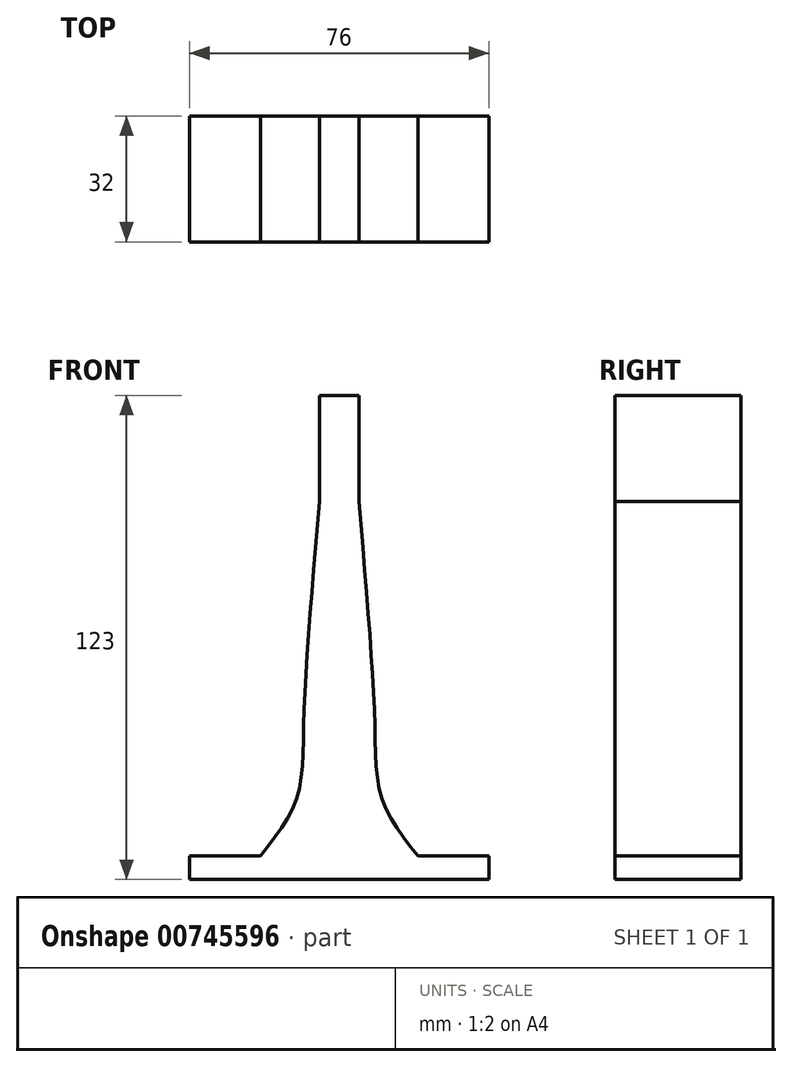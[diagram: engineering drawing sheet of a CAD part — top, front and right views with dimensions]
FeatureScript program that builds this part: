
annotation { "Feature Type Name" : "Feature", "Feature Type Description" : "" }
export const myFeature = defineFeature(function(context is Context, id is Id, definition is map)
    precondition{}
    {
        {
            var Q0;
            Q0=qCreatedBy(makeId("Front.planeOp"),FACE);
            var sketch = newSketch(context, id + "F0", { "sketchPlane" : qUnion([Q0])});
            skLineSegment(sketch, "E0", {"start": v(-38, -61.5) * mm, "end": v(38, -61.5) * mm});
            skLineSegment(sketch, "E1", {"start": v(38, -61.5) * mm, "end": v(38, -55.5) * mm});
            skLineSegment(sketch, "E2", {"start": v(38, -55.5) * mm, "end": v(-38, -55.5) * mm});
            skLineSegment(sketch, "E3", {"start": v(-38, -55.5) * mm, "end": v(-38, -61.5) * mm});
            skLineSegment(sketch, "E4", {"start": v(-5, 61.5) * mm, "end": v(5, 61.5) * mm});
            skFitSpline(sketch, "E5", {"points": [v(-5, 34.5) * mm, v(-9, -21.12) * mm, v(-11, -41.34) * mm, v(-20, -55.5) * mm]});
            skFitSpline(sketch, "E6", {"points": [v(5, 34.5) * mm, v(9, -21.12) * mm, v(11, -41.34) * mm, v(20, -55.5) * mm]});
            skLineSegment(sketch, "E7", {"start": v(5, 61.5) * mm, "end": v(5, -55.5) * mm});
            skLineSegment(sketch, "E8", {"start": v(-5, 61.5) * mm, "end": v(-5, -55.5) * mm});
            skSolve(sketch);
        }
        {
            var Q0;
            Q0=makeQuery(id+"F0.imprint","IMPRINT",FACE,{"disambiguationData":[TD([[makeQuery(id+"F0.imprint","IMPRINT",EDGE,{"derivedFrom":sQuery(id+"F0.wireOp",EDGE,"E0")}),1.0]])]});
            var Q1;
            {var subQ4=sQuery(id+"F0.wireOp",EDGE,"E4");Q1=makeQuery(id+"F0.imprint","IMPRINT",FACE,{"disambiguationData":[TD([[makeQuery(id+"F0.imprint","IMPRINT",EDGE,{"derivedFrom":subQ4}),-1.0]])]});}
            extrude(context, id + "F1", {"entities" : qUnion([Q0, Q1]), "depth" : 32 * mm, "offsetDistance" : 25 * mm});
        }
        {
            var Q0;
            Q0=qCreatedBy(makeId("Front.planeOp"),FACE);
            var sketch = newSketch(context, id + "F2", { "sketchPlane" : qUnion([Q0])});
            skLineSegment(sketch, "E9", {"start": v(-38, -61.5) * mm, "end": v(38, -61.5) * mm});
            skLineSegment(sketch, "E10", {"start": v(38, -61.5) * mm, "end": v(38, -55.5) * mm});
            skLineSegment(sketch, "E11", {"start": v(38, -55.5) * mm, "end": v(-38, -55.5) * mm});
            skLineSegment(sketch, "E12", {"start": v(-38, -55.5) * mm, "end": v(-38, -61.5) * mm});
            skLineSegment(sketch, "E13", {"start": v(-5, 61.5) * mm, "end": v(5, 61.5) * mm});
            skFitSpline(sketch, "E14", {"points": [v(-5, 34.5) * mm, v(-9, -21.12) * mm, v(-11, -41.34) * mm, v(-20, -55.5) * mm]});
            skFitSpline(sketch, "E15", {"points": [v(5, 34.5) * mm, v(9, -21.12) * mm, v(11, -41.34) * mm, v(20, -55.5) * mm]});
            skLineSegment(sketch, "E16", {"start": v(5, 61.5) * mm, "end": v(5, -55.5) * mm});
            skLineSegment(sketch, "E17", {"start": v(-5, 61.5) * mm, "end": v(-5, -55.5) * mm});
            skSolve(sketch);
        }
        {
            var Q0;
            {var subQ0=sQuery(id+"F2.wireOp",EDGE,"E15");Q0=makeQuery(id+"F2.imprint","IMPRINT",FACE,{"disambiguationData":[TD([[makeQuery(id+"F2.imprint","IMPRINT",EDGE,{"derivedFrom":subQ0}),-1.0]])]});}
            var Q1;
            {var subQ0=sQuery(id+"F2.wireOp",EDGE,"E14");Q1=makeQuery(id+"F2.imprint","IMPRINT",FACE,{"disambiguationData":[TD([[makeQuery(id+"F2.imprint","IMPRINT",EDGE,{"derivedFrom":subQ0}),1.0]])]});}
            extrude(context, id + "F3", {"entities" : qUnion([Q0, Q1]), "operationType" : NewBodyOperationType.ADD, "depth" : 32 * mm, "offsetDistance" : 25 * mm});
        }
    });
